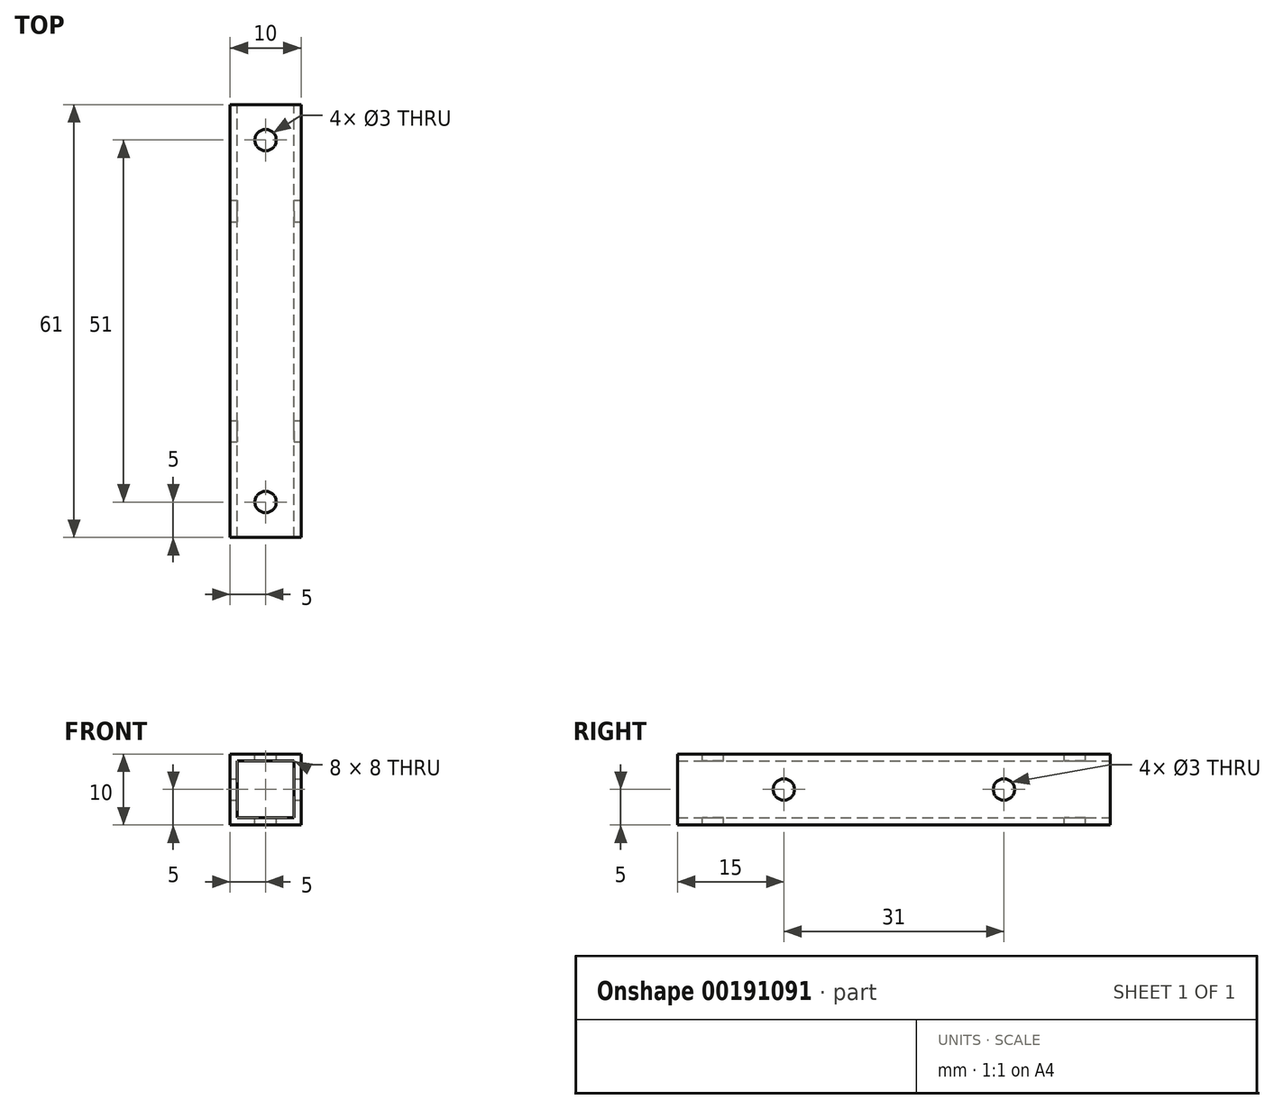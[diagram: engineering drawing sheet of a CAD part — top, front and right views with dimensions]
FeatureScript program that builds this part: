
annotation { "Feature Type Name" : "Feature", "Feature Type Description" : "" }
export const myFeature = defineFeature(function(context is Context, id is Id, definition is map)
    precondition{}
    {
        {
            var Q0;
            Q0=qCreatedBy(makeId("Front.planeOp"),FACE);
            var sketch = newSketch(context, id + "F0", { "sketchPlane" : qUnion([Q0])});
            skLineSegment(sketch, "E0.bottom", {"start": v(-5, -5) * mm, "end": v(5, -5) * mm});
            skLineSegment(sketch, "E0.top", {"start": v(-5, 5) * mm, "end": v(5, 5) * mm});
            skLineSegment(sketch, "E0.left", {"start": v(-5, -5) * mm, "end": v(-5, 5) * mm});
            skLineSegment(sketch, "E0.right", {"start": v(5, -5) * mm, "end": v(5, 5) * mm});
            skPoint(sketch, "E0.middle", {"position": v(0, 0) * mm});
            skLineSegment(sketch, "E1.bottom", {"start": v(-4, -4) * mm, "end": v(4, -4) * mm});
            skLineSegment(sketch, "E1.top", {"start": v(-4, 4) * mm, "end": v(4, 4) * mm});
            skLineSegment(sketch, "E1.left", {"start": v(-4, -4) * mm, "end": v(-4, 4) * mm});
            skLineSegment(sketch, "E1.right", {"start": v(4, -4) * mm, "end": v(4, 4) * mm});
            skSolve(sketch);
        }
        {
            var Q0;
            Q0=qSketchRegion(id+"F0",true);
            extrude(context, id + "F1", {"entities" : qUnion([Q0]), "depth" : 61 * mm});
        }
        {
            var Q0;
            Q0=makeQuery(id+"F1.opExtrude","SWEPT_FACE",FACE,{"disambiguationData":[OSD([sQuery(id+"F0.wireOp",EDGE,"E0.top")])]});
            var sketch = newSketch(context, id + "F2", { "sketchPlane" : qUnion([Q0])});
            skLineSegment(sketch, "E2", {"start": v(0, 0) * mm, "end": v(0, -61) * mm, "construction": true});
            skLineSegment(sketch, "E3", {"start": v(-5, -30.5) * mm, "end": v(5, -30.5) * mm, "construction": true});
            skCircle(sketch, "E4", {"center": v(0, -5) * mm, "radius": 1.5 * mm});
            skCircle(sketch, "E5.MirrorC", {"center": v(0, -56) * mm, "radius": 1.5 * mm});
            skSolve(sketch);
        }
        {
            var Q0;
            Q0=qSketchRegion(id+"F2",true);
            extrude(context, id + "F3", {"entities" : qUnion([Q0]), "operationType" : NewBodyOperationType.REMOVE, "oppositeDirection" : true, "depth" : 25 * mm});
        }
        {
            var Q0;
            Q0=makeQuery(id+"F1.opExtrude","SWEPT_FACE",FACE,{"disambiguationData":[OSD([sQuery(id+"F0.wireOp",EDGE,"E0.right")])]});
            var sketch = newSketch(context, id + "F4", { "sketchPlane" : qUnion([Q0])});
            skLineSegment(sketch, "E6", {"start": v(-61, 0) * mm, "end": v(0, 0) * mm, "construction": true});
            skLineSegment(sketch, "E7", {"start": v(-30.5, 5) * mm, "end": v(-30.5, -5) * mm, "construction": true});
            skCircle(sketch, "E8", {"center": v(-46, 0) * mm, "radius": 1.5 * mm});
            skCircle(sketch, "E9.MirrorC", {"center": v(-15, 0) * mm, "radius": 1.5 * mm});
            skSolve(sketch);
        }
        {
            var Q0;
            Q0=qSketchRegion(id+"F4",true);
            extrude(context, id + "F5", {"entities" : qUnion([Q0]), "operationType" : NewBodyOperationType.REMOVE, "oppositeDirection" : true, "depth" : 25 * mm});
        }
    });
